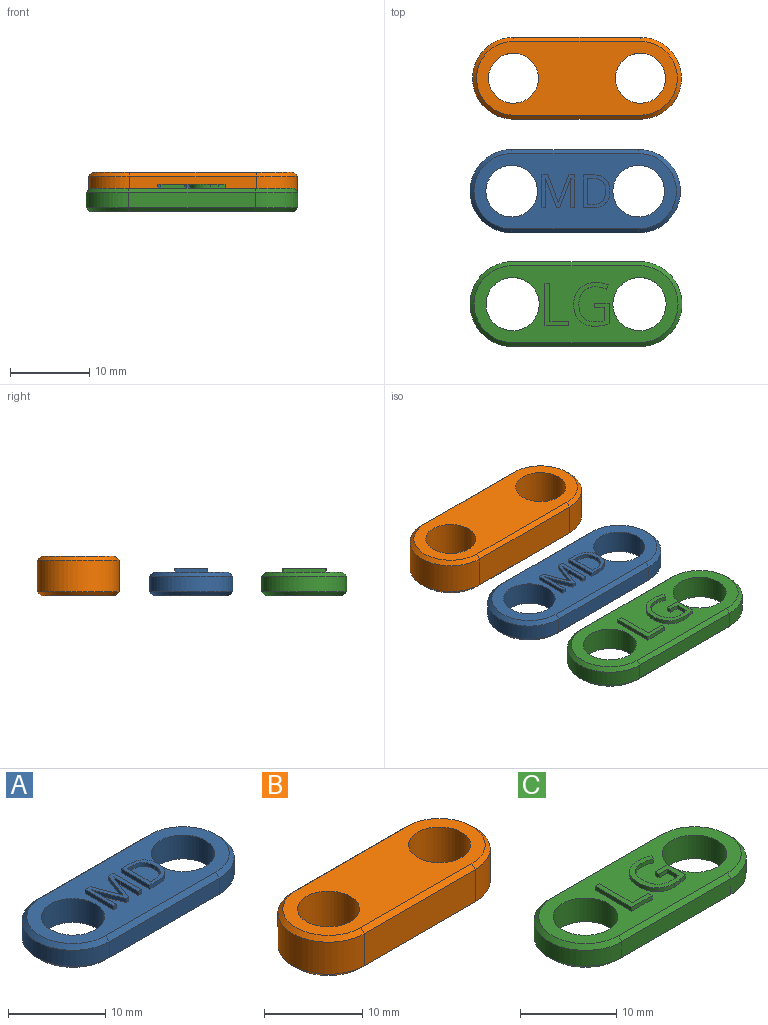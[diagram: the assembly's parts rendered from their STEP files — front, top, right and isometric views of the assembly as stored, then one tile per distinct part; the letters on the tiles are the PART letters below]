
ASSEMBLY  parts=3 mates=2
PART A: 51 faces, bbox 26.5x10.5x3.5 mm
  f0: plane 25.5x9.5mm, normal (0,0,1), area 137mm2, adj f4,f6,f8,f9,f10,f11,f16,f17
  f1: cylinder r=5.25mm len=10.5mm, axis (0,0,-1), area 33mm2, adj f2,f5,f9,f13
  f2: plane 16x2mm, normal (0,1,0), area 32mm2, adj f1,f3,f11,f15
  f3: cylinder r=5.25mm len=10.5mm, axis (0,0,-1), area 33mm2, adj f2,f5,f10,f14
  f4: cylinder r=3.25mm len=6.5mm, axis (0,0,-1), area 61.3mm2, adj f0,f7
  f5: plane 16x2mm, normal (0,-1,0), area 32mm2, adj f1,f3,f8,f12
  f6: cylinder r=3.25mm len=6.5mm, axis (0,0,-1), area 61.3mm2, adj f0,f7
  f7: plane 25.5x9.5mm, normal (0,0,-1), area 156.5mm2, adj f4,f6,f12,f13,f14,f15
  f8: plane 16x0.5mm, normal (0,-0.71,0.71), area 11.3mm2, adj f0,f5,f9,f10
  f9: cone r=5.25mm half-angle=45deg, axis (0,0,-1), area 11.1mm2, adj f0,f1,f8,f11
  f10: cone r=5.25mm half-angle=45deg, axis (0,0,-1), area 11.1mm2, adj f0,f3,f8,f11
  f11: plane 16x0.5mm, normal (0,0.71,0.71), area 11.3mm2, adj f0,f2,f9,f10
  f12: plane 16x0.5mm, normal (0,-0.71,-0.71), area 11.3mm2, adj f5,f7,f13,f14
  f13: cone r=4.75mm half-angle=45deg, axis (0,0,1), area 11.1mm2, adj f1,f7,f12,f15
  f14: cone r=4.75mm half-angle=45deg, axis (0,0,1), area 11.1mm2, adj f3,f7,f12,f15
  f15: plane 16x0.5mm, normal (0,0.71,-0.71), area 11.3mm2, adj f2,f7,f13,f14
  f16: plane 3.68x1.41mm, normal (-0.93,-0.36,0), area 2mm2, adj f0,f17,f33,f34
  f17: plane 0.5x0.39mm, normal (0,-1,0), area 0.2mm2, adj f0,f16,f18,f34
  f18: plane 3.67x1.42mm, normal (0.93,-0.36,0), area 2mm2, adj f0,f17,f19,f34
  f19: plane 0.5x0.02mm, normal (0,-1,0), area 0mm2, adj f0,f18,f20,f34
  f20: extruded ~1x0.5mm, area 0.5mm2, adj f0,f19,f21,f34
  f21: plane 2.67x0.5mm, normal (-1,0,0), area 1.3mm2, adj f0,f20,f22,f34
  f22: plane 0.5x0.48mm, normal (0,-1,0), area 0.2mm2, adj f0,f21,f23,f34
  f23: plane 4.15x0.5mm, normal (1,0,0), area 2.1mm2, adj f0,f22,f24,f34
  f24: plane 0.72x0.5mm, normal (0,1,0), area 0.4mm2, adj f0,f23,f25,f34
  f25: plane 3.42x1.32mm, normal (-0.93,0.36,0), area 1.8mm2, adj f0,f24,f26,f34
  f26: plane 0.5x0.02mm, normal (0,1,0), area 0mm2, adj f0,f25,f27,f34
  f27: plane 3.42x1.31mm, normal (0.93,0.36,0), area 1.8mm2, adj f0,f26,f28,f34
  f28: plane 0.73x0.5mm, normal (0,1,0), area 0.4mm2, adj f0,f27,f29,f34
  f29: plane 4.15x0.5mm, normal (-1,0,0), area 2.1mm2, adj f0,f28,f30,f34
  f30: plane 0.5x0.45mm, normal (0,-1,0), area 0.2mm2, adj f0,f29,f31,f34
  f31: plane 2.64x0.5mm, normal (1,0,0), area 1.3mm2, adj f0,f30,f32,f34
  f32: extruded ~1.04x0.5mm, area 0.5mm2, adj f0,f31,f33,f34
  f33: plane 0.5x0.02mm, normal (0,-1,0), area 0mm2, adj f0,f16,f32,f34
  f34: plane 4.15x4.11mm, normal (0,0,1), area 7.4mm2, adj f16,f17,f18,f19,f20,f21,f22,f23
  f35: extruded ~1.22x0.5mm, area 0.7mm2, adj f36,f48,f49,f50
  f36: extruded ~1.25x0.5mm, area 0.7mm2, adj f35,f37,f49,f50
  f37: extruded ~1.3x0.5mm, area 0.7mm2, adj f36,f38,f49,f50
  f38: plane 0.59x0.5mm, normal (0,1,0), area 0.3mm2, adj f37,f39,f49,f50
  f39: plane 3.31x0.5mm, normal (1,0,0), area 1.7mm2, adj f38,f40,f49,f50
  f40: plane 0.7x0.5mm, normal (0,-1,0), area 0.4mm2, adj f39,f48,f49,f50
  f41: extruded ~1.57x0.56mm, area 0.9mm2, adj f0,f42,f47,f49
  f42: extruded ~1.5x0.54mm, area 0.8mm2, adj f0,f41,f43,f49
  f43: extruded ~1.5x0.54mm, area 0.8mm2, adj f0,f42,f44,f49
  f44: plane 1.27x0.5mm, normal (0,1,0), area 0.6mm2, adj f0,f43,f45,f49
  f45: plane 4.15x0.5mm, normal (-1,0,0), area 2.1mm2, adj f0,f44,f46,f49
  f46: plane 1.15x0.5mm, normal (0,-1,0), area 0.6mm2, adj f0,f45,f47,f49
  f47: extruded ~1.6x0.54mm, area 0.9mm2, adj f0,f41,f46,f49
  f48: extruded ~1.21x0.5mm, area 0.7mm2, adj f35,f40,f49,f50
  f49: plane 4.15x3.31mm, normal (0,0,1), area 5.4mm2, adj f35,f36,f37,f38,f39,f40,f41,f42
  f50: plane 3.31x2.32mm, normal (0,0,1), area 6.7mm2, adj f35,f36,f37,f38,f39,f40,f48
PART B: 16 faces, bbox 26.3x10.3x5 mm
  f0: cylinder r=5.15mm len=10.3mm, axis (0,0,-1), area 64.7mm2, adj f1,f4,f9,f13
  f1: plane 16x4mm, normal (0,1,0), area 64mm2, adj f0,f2,f11,f15
  f2: cylinder r=5.15mm len=10.3mm, axis (0,0,-1), area 64.7mm2, adj f1,f4,f10,f14
  f3: cylinder r=3.15mm len=6.3mm, axis (0,0,-1), area 99mm2, adj f6,f7
  f4: plane 16x4mm, normal (0,-1,0), area 64mm2, adj f0,f2,f8,f12
  f5: cylinder r=3.15mm len=6.3mm, axis (0,0,-1), area 99mm2, adj f6,f7
  f6: plane 25.3x9.3mm, normal (0,0,1), area 154.4mm2, adj f3,f5,f8,f9,f10,f11
  f7: plane 25.3x9.3mm, normal (0,0,-1), area 154.4mm2, adj f3,f5,f12,f13,f14,f15
  f8: plane 16x0.5mm, normal (0,-0.71,0.71), area 11.3mm2, adj f4,f6,f9,f10
  f9: cone r=5.15mm half-angle=45deg, axis (0,0,-1), area 10.9mm2, adj f0,f6,f8,f11
  f10: cone r=5.15mm half-angle=45deg, axis (0,0,-1), area 10.9mm2, adj f2,f6,f8,f11
  f11: plane 16x0.5mm, normal (0,0.71,0.71), area 11.3mm2, adj f1,f6,f9,f10
  f12: plane 16x0.5mm, normal (0,-0.71,-0.71), area 11.3mm2, adj f4,f7,f13,f14
  f13: cone r=4.65mm half-angle=45deg, axis (0,0,1), area 10.9mm2, adj f0,f7,f12,f15
  f14: cone r=4.65mm half-angle=45deg, axis (0,0,1), area 10.9mm2, adj f2,f7,f12,f15
  f15: plane 16x0.5mm, normal (0,0.71,-0.71), area 11.3mm2, adj f1,f7,f13,f14
PART C: 44 faces, bbox 26.7x10.7x3.5 mm
  f0: plane 25.7x9.7mm, normal (0,0,1), area 145.2mm2, adj f4,f6,f8,f9,f10,f11,f16,f17
  f1: cylinder r=5.35mm len=10.7mm, axis (0,0,-1), area 33.6mm2, adj f2,f5,f9,f13
  f2: plane 16x2mm, normal (0,1,0), area 32mm2, adj f1,f3,f11,f15
  f3: cylinder r=5.35mm len=10.7mm, axis (0,0,-1), area 33.6mm2, adj f2,f5,f10,f14
  f4: cylinder r=3.35mm len=6.7mm, axis (0,0,-1), area 63.1mm2, adj f0,f7
  f5: plane 16x2mm, normal (0,-1,0), area 32mm2, adj f1,f3,f8,f12
  f6: cylinder r=3.35mm len=6.7mm, axis (0,0,-1), area 63.1mm2, adj f0,f7
  f7: plane 25.7x9.7mm, normal (0,0,-1), area 158.6mm2, adj f4,f6,f12,f13,f14,f15
  f8: plane 16x0.5mm, normal (0,-0.71,0.71), area 11.3mm2, adj f0,f5,f9,f10
  f9: cone r=5.35mm half-angle=45deg, axis (0,0,-1), area 11.3mm2, adj f0,f1,f8,f11
  f10: cone r=5.35mm half-angle=45deg, axis (0,0,-1), area 11.3mm2, adj f0,f3,f8,f11
  f11: plane 16x0.5mm, normal (0,0.71,0.71), area 11.3mm2, adj f0,f2,f9,f10
  f12: plane 16x0.5mm, normal (0,-0.71,-0.71), area 11.3mm2, adj f5,f7,f13,f14
  f13: cone r=4.85mm half-angle=45deg, axis (0,0,1), area 11.3mm2, adj f1,f7,f12,f15
  f14: cone r=4.85mm half-angle=45deg, axis (0,0,1), area 11.3mm2, adj f3,f7,f12,f15
  f15: plane 16x0.5mm, normal (0,0.71,-0.71), area 11.3mm2, adj f2,f7,f13,f14
  f16: plane 5.36x0.5mm, normal (-1,0,0), area 2.7mm2, adj f0,f17,f21,f22
  f17: plane 2.99x0.5mm, normal (0,-1,0), area 1.5mm2, adj f0,f16,f18,f22
  f18: plane 0.56x0.5mm, normal (1,0,0), area 0.3mm2, adj f0,f17,f19,f22
  f19: plane 2.37x0.5mm, normal (0,1,0), area 1.2mm2, adj f0,f18,f20,f22
  f20: plane 4.8x0.5mm, normal (1,0,0), area 2.4mm2, adj f0,f19,f21,f22
  f21: plane 0.62x0.5mm, normal (0,1,0), area 0.3mm2, adj f0,f16,f20,f22
  f22: plane 5.36x2.99mm, normal (0,0,1), area 4.7mm2, adj f16,f17,f18,f19,f20,f21
  f23: plane 1.82x0.5mm, normal (0,1,0), area 0.9mm2, adj f0,f24,f42,f43
  f24: plane 0.56x0.5mm, normal (-1,0,0), area 0.3mm2, adj f0,f23,f25,f43
  f25: plane 1.2x0.5mm, normal (0,-1,0), area 0.6mm2, adj f0,f24,f26,f43
  f26: plane 1.65x0.5mm, normal (-1,0,0), area 0.8mm2, adj f0,f25,f27,f43
  f27: extruded ~1.09x0.5mm, area 0.5mm2, adj f0,f26,f28,f43
  f28: extruded ~1.56x0.56mm, area 0.9mm2, adj f0,f27,f29,f43
  f29: extruded ~1.65x0.53mm, area 0.9mm2, adj f0,f28,f30,f43
  f30: extruded ~1.62x0.55mm, area 0.9mm2, adj f0,f29,f31,f43
  f31: extruded ~1.53x0.58mm, area 0.8mm2, adj f0,f30,f32,f43
  f32: extruded ~1.4x0.5mm, area 0.7mm2, adj f0,f31,f33,f43
  f33: plane 0.55x0.5mm, normal (0.92,-0.4,0), area 0.3mm2, adj f0,f32,f34,f43
  f34: extruded ~1.6x0.5mm, area 0.8mm2, adj f0,f33,f35,f43
  f35: extruded ~1.48x0.5mm, area 0.8mm2, adj f0,f34,f36,f43
  f36: extruded ~0.97x0.96mm, area 0.7mm2, adj f0,f35,f37,f43
  f37: extruded ~1.47x0.5mm, area 0.8mm2, adj f0,f36,f38,f43
  f38: extruded ~2.03x0.68mm, area 1.1mm2, adj f0,f37,f39,f43
  f39: extruded ~1.89x0.72mm, area 1mm2, adj f0,f38,f40,f43
  f40: extruded ~1.02x0.5mm, area 0.5mm2, adj f0,f39,f41,f43
  f41: extruded ~0.87x0.5mm, area 0.4mm2, adj f0,f40,f42,f43
  f42: plane 2.61x0.5mm, normal (1,0,0), area 1.3mm2, adj f0,f23,f41,f43
  f43: plane 5.51x4.46mm, normal (0,0,1), area 8.7mm2, adj f23,f24,f25,f26,f27,f28,f29,f30
PLACE A at identity fixed
PLACE B t=(0.23,14.23,0)mm
PLACE C t=(0.11,-14.23,0)mm
MATE planar A.f7 <-> B.f7  axis (0,0,-1) through (0,0,0)mm
MATE planar A.f7 <-> C.f7  axis (0,0,-1) through (0,0,0)mm
